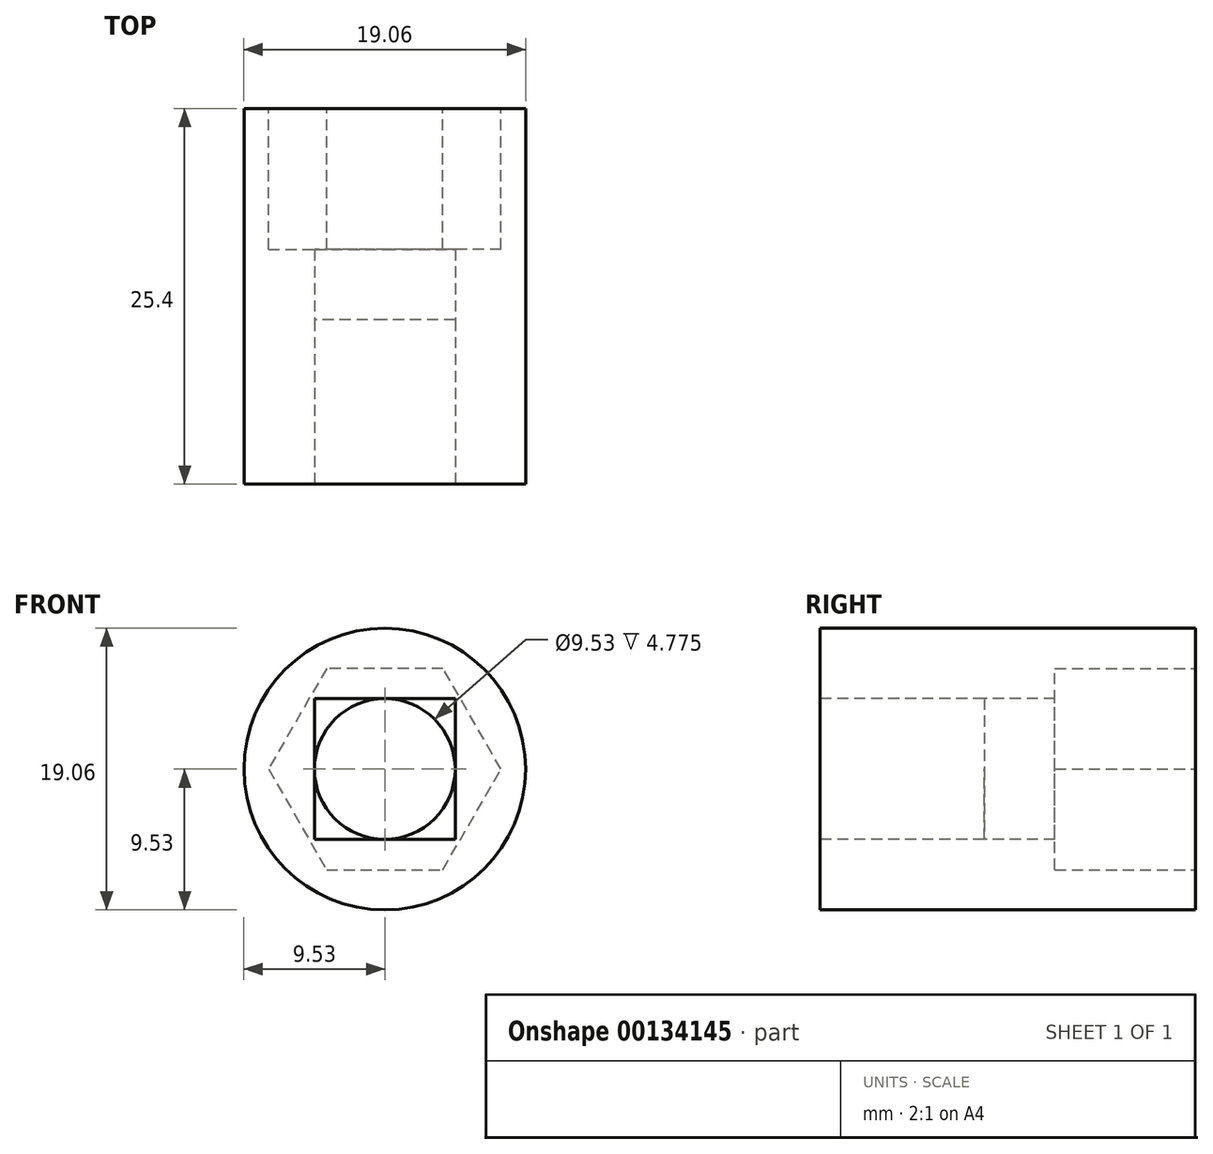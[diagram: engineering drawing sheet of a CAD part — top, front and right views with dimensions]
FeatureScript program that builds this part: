
annotation { "Feature Type Name" : "Feature", "Feature Type Description" : "" }
export const myFeature = defineFeature(function(context is Context, id is Id, definition is map)
    precondition{}
    {
        {
            var Q0;
            Q0=qCreatedBy(makeId("Front.planeOp"),FACE);
            var sketch = newSketch(context, id + "F0", { "sketchPlane" : qUnion([Q0])});
            skCircle(sketch, "E0", {"center": v(0, 0) * mm, "radius": 9.53 * mm});
            skSolve(sketch);
        }
        {
            var Q0;
            Q0=makeQuery(id+"F0.imprint","IMPRINT",FACE,{"disambiguationData":[TD([[makeQuery(id+"F0.imprint","IMPRINT",EDGE,{"derivedFrom":sQuery(id+"F0.wireOp",EDGE,"E0")}),1.0]])]});
            extrude(context, id + "F1", {"entities" : qUnion([Q0]), "depth" : 25.4 * mm});
        }
        {
            var Q0;
            Q0=makeQuery(id+"F1.opExtrude","CAP_FACE",FACE,{"disambiguationData":[OSD([sQuery(id+"F0.wireOp",EDGE,"E0")])],"isStart":false});
            var sketch = newSketch(context, id + "F2", { "sketchPlane" : qUnion([Q0])});
            skLineSegment(sketch, "E1.bottom", {"start": v(4.76, 4.76) * mm, "end": v(-4.76, 4.76) * mm});
            skLineSegment(sketch, "E1.top", {"start": v(4.76, -4.76) * mm, "end": v(-4.76, -4.76) * mm});
            skLineSegment(sketch, "E1.left", {"start": v(4.76, 4.76) * mm, "end": v(4.76, -4.76) * mm});
            skLineSegment(sketch, "E1.right", {"start": v(-4.76, 4.76) * mm, "end": v(-4.76, -4.76) * mm});
            skPoint(sketch, "E1.middle", {"position": v(0, 0) * mm});
            skCircle(sketch, "E2", {"center": v(0, 0) * mm, "radius": 4.76 * mm});
            skSolve(sketch);
        }
        {
            var Q0;
            {var subQ0=sQuery(id+"F2.wireOp",EDGE,"E2");var subQ1=makeQuery(id+"F2.imprint","INTERSECT",VERTEX,{"derivedFrom":[sQuery(id+"F2.wireOp",EDGE,"E1.bottom"),subQ0]});Q0=makeQuery(id+"F2.imprint","IMPRINT",FACE,{"disambiguationData":[TD([[makeQuery(id+"F2.imprint","IMPRINT",EDGE,{"disambiguationData":[TD([[subQ1,1.0]])],"derivedFrom":subQ0}),1.0]])]});}
            extrude(context, id + "F3", {"entities" : qUnion([Q0]), "operationType" : NewBodyOperationType.REMOVE, "endBound" : BoundingType.THROUGH_ALL, "oppositeDirection" : true, "depth" : 25.4 * mm});
        }
        {
            var Q0;
            Q0 = qSketchRegion(id + "F2", true);
            extrude(context, id + "F4", {"entities" : qUnion([Q0]), "operationType" : NewBodyOperationType.REMOVE, "oppositeDirection" : true, "depth" : 11.1 * mm});
        }
        {
            var Q0;
            Q0=makeQuery(id+"F1.opExtrude","CAP_FACE",FACE,{"disambiguationData":[OSD([sQuery(id+"F0.wireOp",EDGE,"E0")])],"isStart":true});
            var sketch = newSketch(context, id + "F5", { "sketchPlane" : qUnion([Q0])});
            skCircle(sketch, "E3.cCircle", {"center": v(0, 0) * mm, "radius": 6.81 * mm, "construction": true});
            skLineSegment(sketch, "E3.0", {"start": v(-3.93, 6.81) * mm, "end": v(3.93, 6.81) * mm});
            skLineSegment(sketch, "E3.1", {"start": v(3.93, 6.81) * mm, "end": v(7.86, 0) * mm});
            skLineSegment(sketch, "E3.2", {"start": v(7.86, 0) * mm, "end": v(3.93, -6.81) * mm});
            skLineSegment(sketch, "E3.3", {"start": v(3.93, -6.81) * mm, "end": v(-3.93, -6.81) * mm});
            skLineSegment(sketch, "E3.4", {"start": v(-3.93, -6.81) * mm, "end": v(-7.86, 0) * mm});
            skLineSegment(sketch, "E3.5", {"start": v(-7.86, 0) * mm, "end": v(-3.93, 6.81) * mm});
            skPoint(sketch, "E3.0.midPoint", {"position": v(0, 6.81) * mm});
            skSolve(sketch);
        }
        {
            var Q0;
            Q0=makeQuery(id+"F5.imprint","IMPRINT",FACE,{"disambiguationData":[TD([[makeQuery(id+"F5.imprint","IMPRINT",EDGE,{"derivedFrom":sQuery(id+"F5.wireOp",EDGE,"E3.0")}),-1.0]])]});
            extrude(context, id + "F6", {"entities" : qUnion([Q0]), "operationType" : NewBodyOperationType.REMOVE, "oppositeDirection" : true, "depth" : 9.52 * mm});
        }
    });
